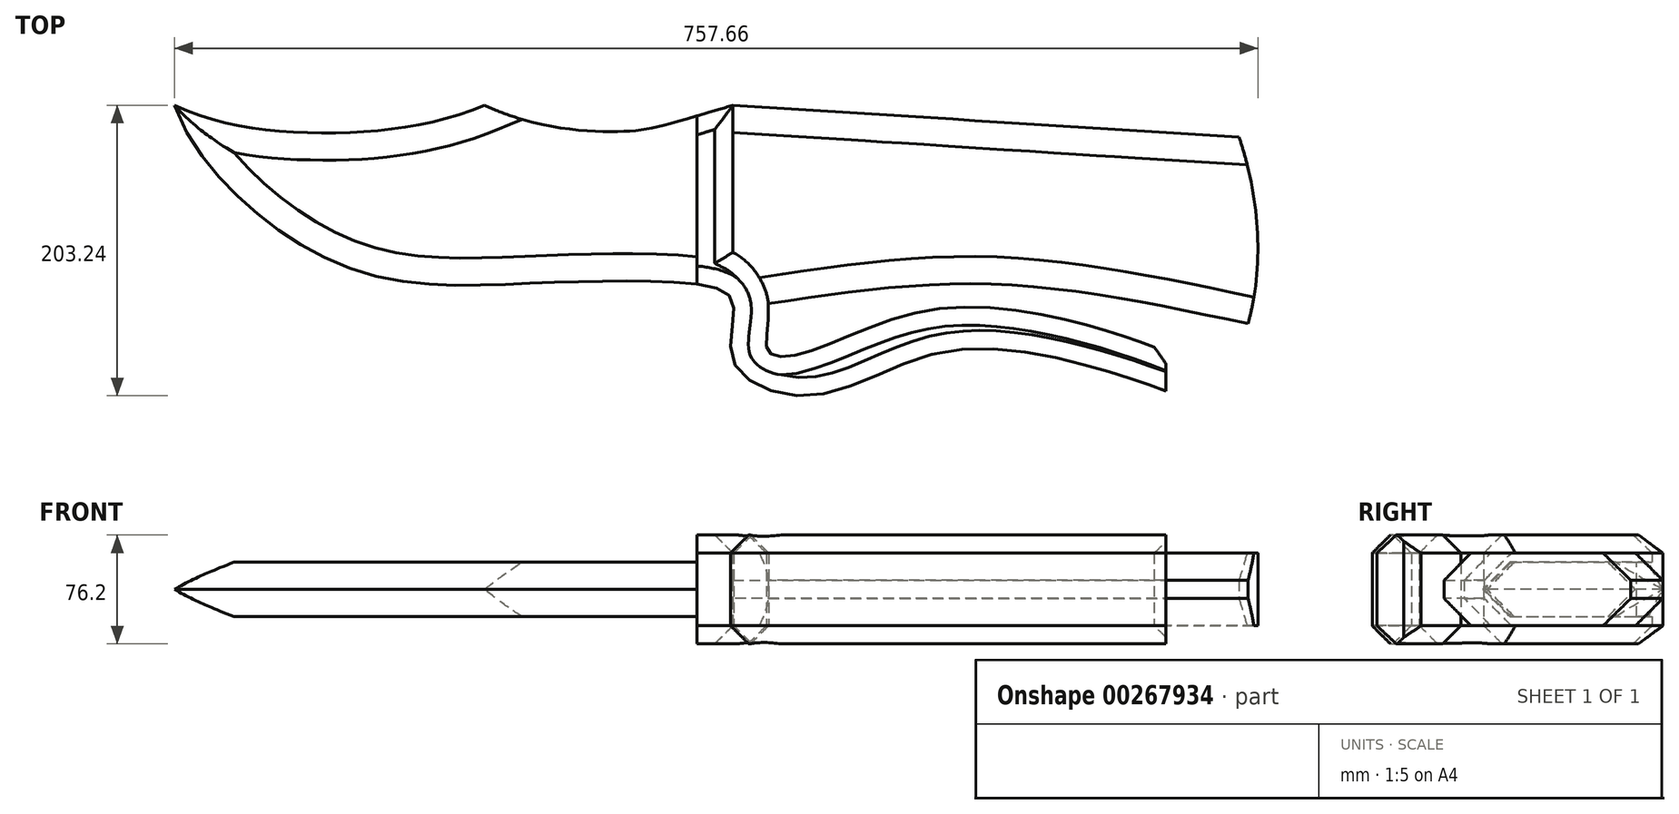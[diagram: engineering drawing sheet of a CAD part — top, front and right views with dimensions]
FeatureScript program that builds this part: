
annotation { "Feature Type Name" : "Feature", "Feature Type Description" : "" }
export const myFeature = defineFeature(function(context is Context, id is Id, definition is map)
    precondition{}
    {
        {
            var Q0;
            Q0=qCreatedBy(makeId("Top.planeOp"),FACE);
            var sketch = newSketch(context, id + "F0", { "sketchPlane" : qUnion([Q0])});
            skLineSegment(sketch, "E0", {"start": v(-312.99, 0) * mm, "end": v(309.79, 0) * mm, "construction": true});
            skFitSpline(sketch, "E1", {"points": [v(-390.57, 71.02) * mm, v(-281.02, -37.71) * mm, v(-144.16, -53.68) * mm, v(-25.36, -54.16) * mm, v(0, -66.9) * mm, v(0, -107.66) * mm, v(55.05, -132) * mm, v(147.04, -101.58) * mm, v(254.25, -112.99) * mm, v(302.91, -128.95) * mm], "startDerivative": vector(248.82, -780.69) * mm, "endDerivative": vector(469.88, -168.28) * mm});
            skFitSpline(sketch, "E2", {"points": [v(-390.57, 71.02) * mm, v(-289.27, 51.71) * mm, v(-173.8, 71.02) * mm], "startDerivative": vector(205.2, -95.24) * mm, "endDerivative": vector(228.12, 93.34) * mm});
            skFitSpline(sketch, "E3", {"points": [v(-173.8, 71.02) * mm, v(-76.55, 52.73) * mm, v(0, 71.02) * mm], "startDerivative": vector(205.55, -96.03) * mm, "endDerivative": vector(305.16, 88.83) * mm});
            skLineSegment(sketch, "E4", {"start": v(302.91, -128.95) * mm, "end": v(302.91, -101.24) * mm});
            skFitSpline(sketch, "E5", {"points": [v(302.91, -101.24) * mm, v(251.65, -84.02) * mm, v(140.22, -71.87) * mm, v(53.1, -101.24) * mm, v(24.74, -101.24) * mm, v(24.74, -67.81) * mm, v(0, -31.88) * mm], "startDerivative": vector(-272.2, 102.52) * mm, "endDerivative": vector(-256.8, 132.41) * mm});
            skLineSegment(sketch, "E6", {"start": v(-25.36, -54.16) * mm, "end": v(-25.36, 63.56) * mm});
            skLineSegment(sketch, "E7", {"start": v(0, -31.88) * mm, "end": v(0, 71.02) * mm});
            skFitSpline(sketch, "E8", {"points": [v(24.74, -67.81) * mm, v(182.6, -54.16) * mm, v(360.23, -81.83) * mm], "startDerivative": vector(320.51, 47.4) * mm, "endDerivative": vector(342.24, -71.88) * mm});
            skFitSpline(sketch, "E9", {"points": [v(0, 71.02) * mm, v(353.97, 48.69) * mm], "startDerivative": vector(349.9, -21.11) * mm, "endDerivative": vector(349.9, -21.11) * mm});
            skFitSpline(sketch, "E10", {"points": [v(353.97, 48.69) * mm, v(360.23, -81.83) * mm], "startDerivative": vector(42.34, -124) * mm, "endDerivative": vector(-34.7, -125.63) * mm});
            skSolve(sketch);
        }
        {
            var Q0;
            {var subQ1=sQuery(id+"F0.wireOp",EDGE,"E7");Q0=makeQuery(id+"F0.imprint","IMPRINT",FACE,{"disambiguationData":[TD([[makeQuery(id+"F0.imprint","IMPRINT",EDGE,{"derivedFrom":subQ1}),-1.0]])]});}
            extrude(context, id + "F1", {"entities" : qUnion([Q0]), "depth" : 25.4 * mm, "hasSecondDirection" : true, "secondDirectionOppositeDirection" : true, "secondDirectionDepth" : 25.4 * mm});
        }
        {
            var Q0;
            {var subQ0=sQuery(id+"F0.wireOp",EDGE,"E4");Q0=makeQuery(id+"F0.imprint","IMPRINT",FACE,{"disambiguationData":[TD([[makeQuery(id+"F0.imprint","IMPRINT",EDGE,{"derivedFrom":subQ0}),1.0]])]});}
            extrude(context, id + "F2", {"entities" : qUnion([Q0]), "operationType" : NewBodyOperationType.ADD, "depth" : 38.1 * mm, "hasSecondDirection" : true, "secondDirectionOppositeDirection" : true, "secondDirectionDepth" : 38.1 * mm});
        }
        {
            var Q0;
            {var subQ0=sQuery(id+"F0.wireOp",EDGE,"E2");Q0=makeQuery(id+"F0.imprint","IMPRINT",FACE,{"disambiguationData":[TD([[makeQuery(id+"F0.imprint","IMPRINT",EDGE,{"derivedFrom":subQ0}),-1.0]])]});}
            extrude(context, id + "F3", {"entities" : qUnion([Q0]), "operationType" : NewBodyOperationType.ADD, "depth" : 19.05 * mm, "hasSecondDirection" : true, "secondDirectionOppositeDirection" : true, "secondDirectionDepth" : 19.05 * mm});
        }
        {
            var Q0;
            Q0=makeQuery(id+"F3.opExtrude","CAP_EDGE",EDGE,{"disambiguationData":[OSD([sQuery(id+"F0.wireOp",EDGE,"E2")])],"isStart":false});
            var Q1;
            Q1=makeQuery(id+"F3.opExtrude","CAP_EDGE",EDGE,{"disambiguationData":[OSD([sQuery(id+"F0.wireOp",EDGE,"E1")])],"isStart":false});
            var Q2;
            Q2=makeQuery(id+"F3.opExtrude","CAP_EDGE",EDGE,{"disambiguationData":[OSD([sQuery(id+"F0.wireOp",EDGE,"E1")])],"isStart":true});
            var Q3;
            Q3=makeQuery(id+"F3.opExtrude","CAP_EDGE",EDGE,{"disambiguationData":[OSD([sQuery(id+"F0.wireOp",EDGE,"E2")])],"isStart":true});
            chamfer(context, id + "F4", {"entities" : qUnion([Q0, Q1, Q2, Q3]), "width" : 19.05 * mm, "tangentPropagation" : true});
        }
        {
            var Q0;
            Q0=makeQuery(id+"F1.opExtrude","CAP_EDGE",EDGE,{"disambiguationData":[OSD([sQuery(id+"F0.wireOp",EDGE,"E9")])],"isStart":false});
            var Q1;
            Q1=makeQuery(id+"F1.opExtrude","CAP_EDGE",EDGE,{"disambiguationData":[OSD([sQuery(id+"F0.wireOp",EDGE,"E9")])],"isStart":true});
            var Q2;
            Q2=makeQuery(id+"F1.opExtrude","CAP_EDGE",EDGE,{"disambiguationData":[OSD([sQuery(id+"F0.wireOp",EDGE,"E8")])],"isStart":false});
            var Q3;
            Q3=makeQuery(id+"F1.opExtrude","CAP_EDGE",EDGE,{"disambiguationData":[OSD([sQuery(id+"F0.wireOp",EDGE,"E8")])],"isStart":true});
            chamfer(context, id + "F5", {"entities" : qUnion([Q0, Q1, Q2, Q3]), "width" : 19.05 * mm, "tangentPropagation" : true});
        }
        {
            var Q0;
            Q0=makeQuery(id+"F2.opExtrude","CAP_EDGE",EDGE,{"disambiguationData":[OSD([sQuery(id+"F0.wireOp",EDGE,"E3")])],"isStart":false});
            var Q1;
            Q1=makeQuery(id+"F2.opExtrude","CAP_EDGE",EDGE,{"disambiguationData":[OSD([sQuery(id+"F0.wireOp",EDGE,"E3")])],"isStart":true});
            var Q2;
            Q2=makeQuery(id+"F2.opExtrude","CAP_EDGE",EDGE,{"disambiguationData":[OSD([sQuery(id+"F0.wireOp",EDGE,"E1")])],"isStart":false});
            var Q3;
            Q3=makeQuery(id+"F2.opExtrude","CAP_EDGE",EDGE,{"disambiguationData":[OSD([sQuery(id+"F0.wireOp",EDGE,"E1")])],"isStart":true});
            var Q4;
            Q4=makeQuery(id+"F2.opExtrude","CAP_EDGE",EDGE,{"disambiguationData":[OSD([sQuery(id+"F0.wireOp",EDGE,"E5")])],"isStart":false});
            var Q5;
            Q5=makeQuery(id+"F2.opExtrude","CAP_EDGE",EDGE,{"disambiguationData":[OSD([sQuery(id+"F0.wireOp",EDGE,"E7")])],"isStart":false});
            var Q6;
            Q6=makeQuery(id+"F2.opExtrude","CAP_EDGE",EDGE,{"disambiguationData":[OSD([sQuery(id+"F0.wireOp",EDGE,"E5")])],"isStart":true});
            var Q7;
            Q7=makeQuery(id+"F2.opExtrude","CAP_EDGE",EDGE,{"disambiguationData":[OSD([sQuery(id+"F0.wireOp",EDGE,"E7")])],"isStart":true});
            var Q8;
            Q8=makeQuery(id+"F2.opExtrude","SWEPT_EDGE",EDGE,{"disambiguationData":[OSD([sQuery(id+"F0.wireOp",EDGE,"E4"),sQuery(id+"F0.wireOp",EDGE,"E5")])]});
            chamfer(context, id + "F6", {"entities" : qUnion([Q0, Q1, Q2, Q3, Q4, Q5, Q6, Q7, Q8]), "width" : 12.7 * mm, "tangentPropagation" : true});
        }
    });
